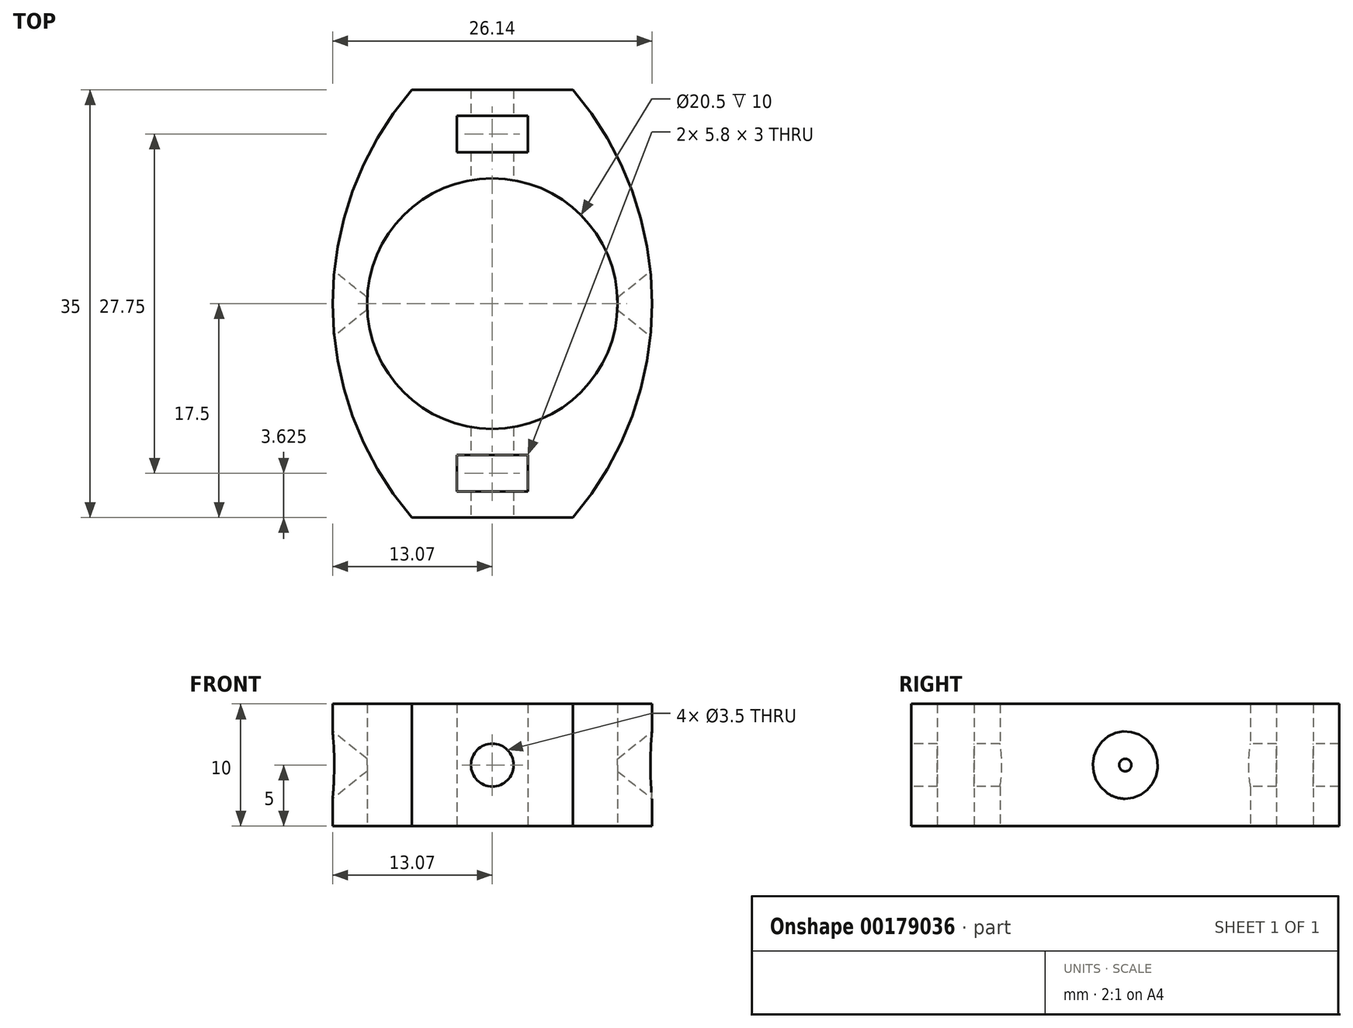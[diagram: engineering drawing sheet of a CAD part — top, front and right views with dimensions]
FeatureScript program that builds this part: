
annotation { "Feature Type Name" : "Feature", "Feature Type Description" : "" }
export const myFeature = defineFeature(function(context is Context, id is Id, definition is map)
    precondition{}
    {
        {
            var Q0;
            Q0=qCreatedBy(makeId("Top.planeOp"),FACE);
            var sketch = newSketch(context, id + "F0", { "sketchPlane" : qUnion([Q0])});
            skCircle(sketch, "E0", {"center": v(0, 0) * mm, "radius": 10.25 * mm});
            skLineSegment(sketch, "E1.bottom", {"start": v(-17.5, 17.5) * mm, "end": v(17.5, 17.5) * mm});
            skLineSegment(sketch, "E1.top", {"start": v(-17.5, -17.5) * mm, "end": v(17.5, -17.5) * mm});
            skLineSegment(sketch, "E1.left", {"start": v(-17.5, 17.5) * mm, "end": v(-17.5, -17.5) * mm});
            skLineSegment(sketch, "E1.right", {"start": v(17.5, 17.5) * mm, "end": v(17.5, -17.5) * mm});
            skLineSegment(sketch, "E2.bottom", {"start": v(2.9, 12.38) * mm, "end": v(-2.9, 12.38) * mm});
            skLineSegment(sketch, "E2.top", {"start": v(2.9, 15.38) * mm, "end": v(-2.9, 15.38) * mm});
            skLineSegment(sketch, "E2.left", {"start": v(2.9, 12.38) * mm, "end": v(2.9, 15.38) * mm});
            skLineSegment(sketch, "E2.right", {"start": v(-2.9, 12.38) * mm, "end": v(-2.9, 15.38) * mm});
            skPoint(sketch, "E2.middle", {"position": v(0, 13.88) * mm});
            skLineSegment(sketch, "E3", {"start": v(0, 10.25) * mm, "end": v(0, 17.5) * mm, "construction": true});
            skPoint(sketch, "E4.MirrorP", {"position": v(0, -13.88) * mm});
            skLineSegment(sketch, "E5.MirrorCS", {"start": v(2.9, -12.38) * mm, "end": v(2.9, -15.38) * mm});
            skLineSegment(sketch, "E6.MirrorCS", {"start": v(2.9, -15.38) * mm, "end": v(-2.9, -15.38) * mm});
            skLineSegment(sketch, "E7.MirrorCS", {"start": v(-2.9, -12.38) * mm, "end": v(-2.9, -15.38) * mm});
            skLineSegment(sketch, "E8.MirrorCS", {"start": v(2.9, -12.38) * mm, "end": v(-2.9, -12.38) * mm});
            skArc(sketch, "E9", {"start": v(-6.59, 17.5) * mm, "mid": v(-13.07, 0) * mm, "end": v(-6.59, -17.5) * mm});
            skArc(sketch, "E10.MirrorCS", {"start": v(6.59, 17.5) * mm, "mid": v(13.07, 0) * mm, "end": v(6.59, -17.5) * mm});
            skSolve(sketch);
        }
        {
            var Q0;
            Q0=makeQuery(id+"F0.imprint","IMPRINT",FACE,{"disambiguationData":[TD([[makeQuery(id+"F0.imprint","IMPRINT",EDGE,{"derivedFrom":sQuery(id+"F0.wireOp",EDGE,"E0")}),-1.0]])]});
            extrude(context, id + "F1", {"entities" : qUnion([Q0]), "depth" : 10 * mm, "offsetDistance" : 25 * mm});
        }
        {
            var Q0;
            Q0=qCreatedBy(makeId("Right.planeOp"),FACE);
            var sketch = newSketch(context, id + "F2", { "sketchPlane" : qUnion([Q0])});
            skCircle(sketch, "E11", {"center": v(0, 5) * mm, "radius": 0.5 * mm});
            skPoint(sketch, "E11.centerSnap0", {"position": v(-17.5, 5) * mm});
            skSolve(sketch);
        }
        {
            var Q0;
            Q0 = qSketchRegion(id + "F2", true);
            extrude(context, id + "F3", {"entities" : qUnion([Q0]), "operationType" : NewBodyOperationType.REMOVE, "endBound" : BoundingType.THROUGH_ALL, "oppositeDirection" : true, "depth" : 25 * mm, "offsetDistance" : 25 * mm, "hasSecondDirection" : true, "secondDirectionBound" : SecondDirectionBoundingType.THROUGH_ALL, "secondDirectionOppositeDirection" : false, "secondDirectionDepth" : 25 * mm});
        }
        {
            var Q0;
            Q0=qCreatedBy(makeId("Top.planeOp"),FACE);
            var Q1;
            Q1=sQuery(id+"F2.wireOp",VERTEX,"E11.center");
            cPlane(context, id + "F4", {"entities" : qUnion([Q0, Q1]), "cplaneType" : CPlaneType.PLANE_POINT, "offset" : 25 * mm, "width" : 150 * mm, "height" : 150 * mm});
        }
        {
            var Q0;
            Q0=qCreatedBy(id+"F4.planeOp",FACE);
            var sketch = newSketch(context, id + "F5", { "sketchPlane" : qUnion([Q0])});
            skLineSegment(sketch, "E12", {"start": v(13.06, -0.5) * mm, "end": v(10.24, -0.5) * mm, "construction": true});
            skLineSegment(sketch, "E13", {"start": v(10.24, 0.5) * mm, "end": v(13.06, 0.5) * mm});
            skLineSegment(sketch, "E14", {"start": v(13.12, 0) * mm, "end": v(9.61, 0) * mm});
            skLineSegment(sketch, "E15", {"start": v(9.61, 0) * mm, "end": v(13.12, -2.8) * mm});
            skLineSegment(sketch, "E16", {"start": v(13.12, -2.8) * mm, "end": v(13.12, 0) * mm});
            skLineSegment(sketch, "E17.MirrorCS", {"start": v(-13.12, -2.8) * mm, "end": v(-13.12, 0) * mm});
            skLineSegment(sketch, "E18.MirrorCS", {"start": v(-13.06, -0.5) * mm, "end": v(-10.24, -0.5) * mm, "construction": true});
            skLineSegment(sketch, "E19.MirrorCS", {"start": v(-13.12, 0) * mm, "end": v(-9.61, 0) * mm});
            skLineSegment(sketch, "E20.MirrorCS", {"start": v(-9.61, 0) * mm, "end": v(-13.12, -2.8) * mm});
            skSolve(sketch);
        }
        {
            var Q0;
            Q0=makeQuery(id+"F5.imprint","IMPRINT",FACE,{"disambiguationData":[TD([[makeQuery(id+"F5.imprint","IMPRINT",EDGE,{"derivedFrom":sQuery(id+"F5.wireOp",EDGE,"E14")}),1.0]])]});
            var Q1;
            Q1=makeQuery(id+"F5.imprint","IMPRINT",FACE,{"disambiguationData":[TD([[makeQuery(id+"F5.imprint","IMPRINT",EDGE,{"derivedFrom":sQuery(id+"F5.wireOp",EDGE,"E17.MirrorCS")}),-1.0]])]});
            var Q2;
            Q2=sQuery(id+"F5.wireOp",EDGE,"E14");
            revolve(context, id + "F6", {"operationType" : NewBodyOperationType.REMOVE, "surfaceOperationType" : NewSurfaceOperationType.NEW, "entities" : qUnion([Q0, Q1]), "axis" : qUnion([Q2]), "revolveType" : RevolveType.FULL, "oppositeDirection" : true});
        }
        {
            var Q0;
            Q0=makeQuery(id+"F1.opExtrude","SWEPT_FACE",FACE,{"disambiguationData":[OSD([sQuery(id+"F0.wireOp",EDGE,"E1.top")])]});
            var sketch = newSketch(context, id + "F7", { "sketchPlane" : qUnion([Q0])});
            skCircle(sketch, "E21", {"center": v(0, 5) * mm, "radius": 1.75 * mm});
            skPoint(sketch, "E21.centerSnap0", {"position": v(6.59, 5) * mm});
            skSolve(sketch);
        }
        {
            var Q0;
            Q0 = qSketchRegion(id + "F7", true);
            extrude(context, id + "F8", {"entities" : qUnion([Q0]), "operationType" : NewBodyOperationType.REMOVE, "endBound" : BoundingType.THROUGH_ALL, "oppositeDirection" : true, "depth" : 25 * mm, "offsetDistance" : 25 * mm});
        }
    });
